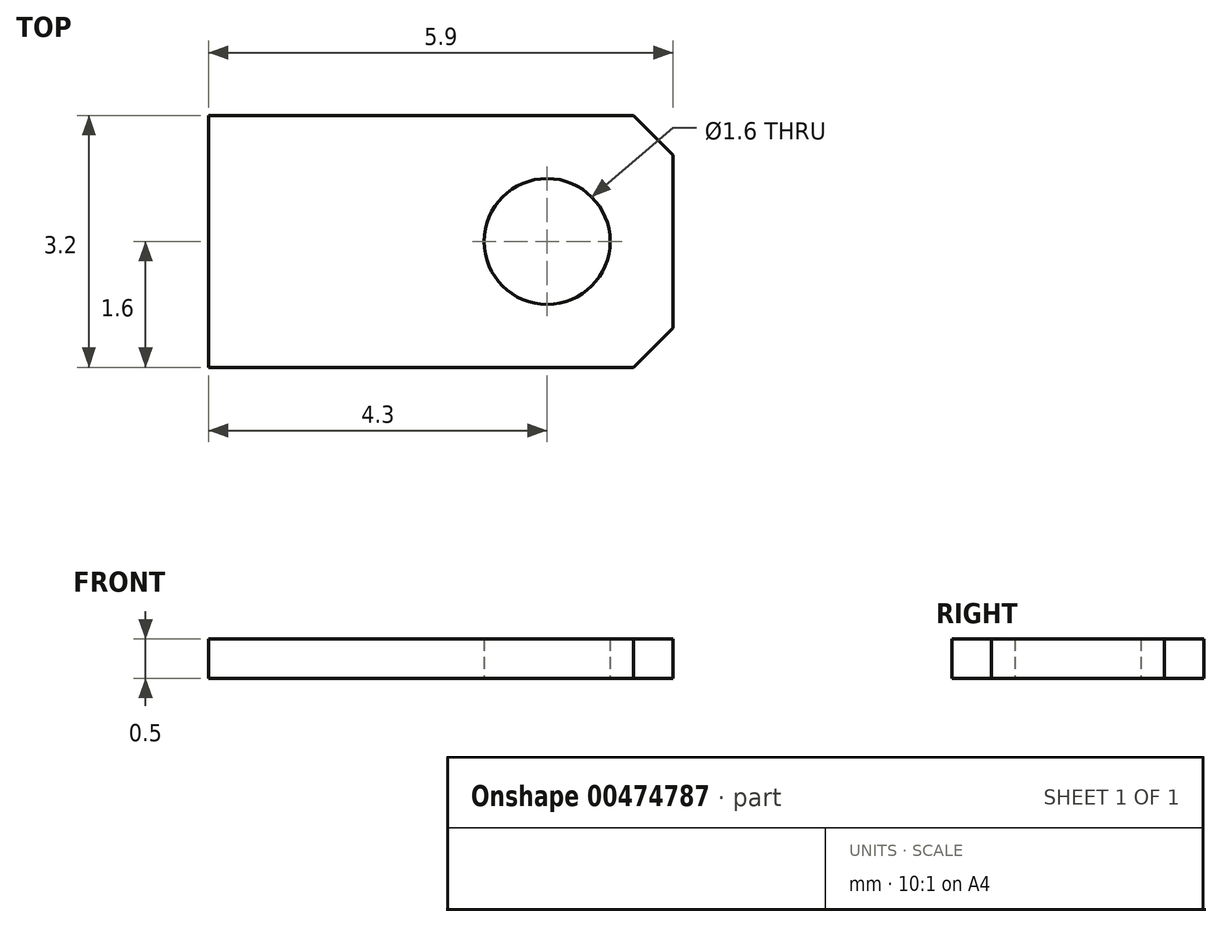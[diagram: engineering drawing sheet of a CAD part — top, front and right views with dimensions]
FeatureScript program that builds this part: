
annotation { "Feature Type Name" : "Feature", "Feature Type Description" : "" }
export const myFeature = defineFeature(function(context is Context, id is Id, definition is map)
    precondition{}
    {
        {
            var Q0;
            Q0=qCreatedBy(makeId("Top.planeOp"),FACE);
            var sketch = newSketch(context, id + "F0", { "sketchPlane" : qUnion([Q0])});
            skLineSegment(sketch, "E0.bottom", {"start": v(0, 0) * mm, "end": v(5.4, 0) * mm});
            skLineSegment(sketch, "E0.top", {"start": v(0, 3.2) * mm, "end": v(5.4, 3.2) * mm});
            skLineSegment(sketch, "E0.left", {"start": v(0, 0) * mm, "end": v(0, 3.2) * mm});
            skLineSegment(sketch, "E0.right", {"start": v(5.9, 0.5) * mm, "end": v(5.9, 2.7) * mm});
            skCircle(sketch, "E1", {"center": v(4.3, 1.6) * mm, "radius": 0.8 * mm});
            skLineSegment(sketch, "E2", {"start": v(0, 1.6) * mm, "end": v(5.9, 1.6) * mm, "construction": true});
            skLineSegment(sketch, "E3", {"start": v(5.4, 3.2) * mm, "end": v(5.9, 2.7) * mm});
            skLineSegment(sketch, "E4", {"start": v(5.4, 0) * mm, "end": v(5.9, 0.5) * mm});
            skPoint(sketch, "E5.orphan", {"position": v(5.9, 3.2) * mm});
            skPoint(sketch, "E6.orphan", {"position": v(5.9, 0) * mm});
            skSolve(sketch);
        }
        {
            var Q0;
            Q0=qSketchRegion(id+"F0",true);
            extrude(context, id + "F1", {"entities" : qUnion([Q0]), "depth" : 0.5 * mm, "offsetDistance" : 25 * mm});
        }
    });
